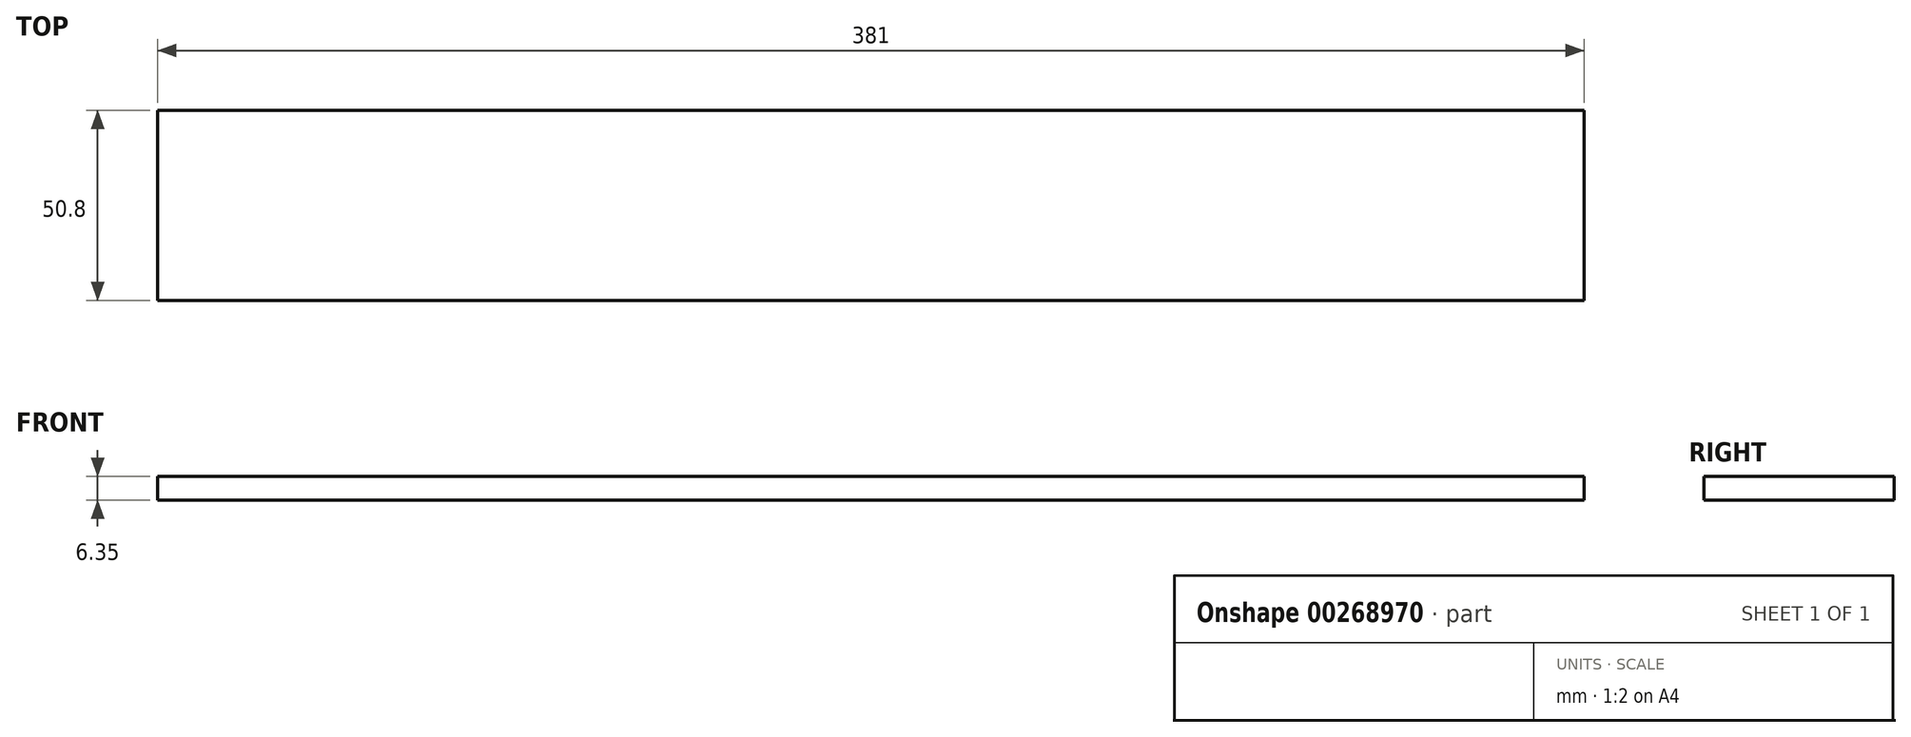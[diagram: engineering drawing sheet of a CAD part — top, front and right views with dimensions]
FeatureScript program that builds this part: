
annotation { "Feature Type Name" : "Feature", "Feature Type Description" : "" }
export const myFeature = defineFeature(function(context is Context, id is Id, definition is map)
    precondition{}
    {
        {
            var Q0;
            Q0=qCreatedBy(makeId("Top.planeOp"),FACE);
            var sketch = newSketch(context, id + "F0", { "sketchPlane" : qUnion([Q0])});
            skLineSegment(sketch, "E0.bottom", {"start": v(-209.96, -14.57) * mm, "end": v(171.04, -14.57) * mm});
            skLineSegment(sketch, "E0.top", {"start": v(-209.96, -65.37) * mm, "end": v(171.04, -65.37) * mm});
            skLineSegment(sketch, "E0.left", {"start": v(-209.96, -14.57) * mm, "end": v(-209.96, -65.37) * mm});
            skLineSegment(sketch, "E0.right", {"start": v(171.04, -14.57) * mm, "end": v(171.04, -65.37) * mm});
            skSolve(sketch);
        }
        {
            var Q0;
            Q0 = qSketchRegion(id + "F0", true);
            extrude(context, id + "F1", {"entities" : qUnion([Q0]), "depth" : 6.35 * mm});
        }
    });
